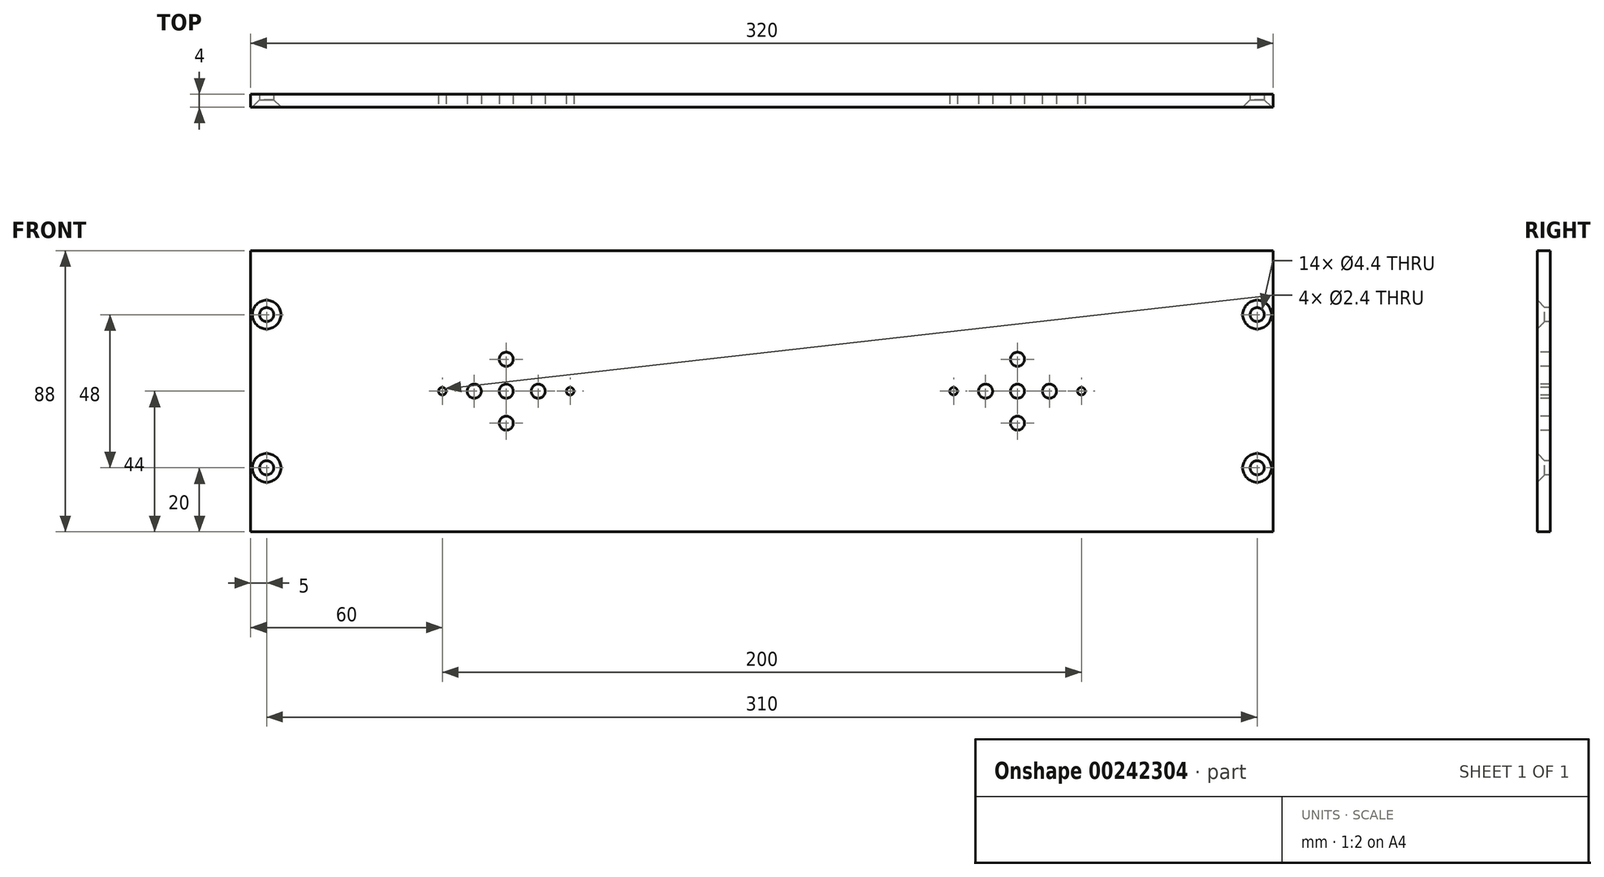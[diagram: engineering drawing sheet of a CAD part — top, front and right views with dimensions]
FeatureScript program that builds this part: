
annotation { "Feature Type Name" : "Feature", "Feature Type Description" : "" }
export const myFeature = defineFeature(function(context is Context, id is Id, definition is map)
    precondition{}
    {
        {
            var Q0;
            Q0=qCreatedBy(makeId("Front.planeOp"),FACE);
            var sketch = newSketch(context, id + "F0", { "sketchPlane" : qUnion([Q0])});
            skLineSegment(sketch, "E0.bottom", {"start": v(160, -44) * mm, "end": v(-160, -44) * mm});
            skLineSegment(sketch, "E0.top", {"start": v(160, 44) * mm, "end": v(-160, 44) * mm});
            skLineSegment(sketch, "E0.left", {"start": v(160, -44) * mm, "end": v(160, 44) * mm});
            skLineSegment(sketch, "E0.right", {"start": v(-160, -44) * mm, "end": v(-160, 44) * mm});
            skPoint(sketch, "E0.middle", {"position": v(0, 0) * mm});
            skSolve(sketch);
        }
        {
            var Q0;
            Q0=makeQuery(id+"F0.imprint","IMPRINT",FACE,{"disambiguationData":[TD([[makeQuery(id+"F0.imprint","IMPRINT",EDGE,{"derivedFrom":sQuery(id+"F0.wireOp",EDGE,"E0.bottom")}),-1.0]])]});
            extrude(context, id + "F1", {"entities" : qUnion([Q0]), "endBound" : BoundingType.SYMMETRIC, "depth" : 4 * mm});
        }
        {
            var Q0;
            Q0=makeQuery(id+"F1.opExtrude","CAP_FACE",FACE,{"disambiguationData":[OSD([sQuery(id+"F0.wireOp",EDGE,"E0.bottom"),sQuery(id+"F0.wireOp",EDGE,"E0.top"),sQuery(id+"F0.wireOp",EDGE,"E0.left"),sQuery(id+"F0.wireOp",EDGE,"E0.right")])],"isStart":false});
            var sketch = newSketch(context, id + "F2", { "sketchPlane" : qUnion([Q0])});
            skCircle(sketch, "E1", {"center": v(-155, -24) * mm, "radius": 2 * mm});
            skCircle(sketch, "E2.0.1.0", {"center": v(-155, 24) * mm, "radius": 2 * mm});
            skCircle(sketch, "E2.1.0.0", {"center": v(155, -24) * mm, "radius": 2 * mm});
            skCircle(sketch, "E2.1.1.0", {"center": v(155, 24) * mm, "radius": 2 * mm});
            skLineSegment(sketch, "E2.direction1", {"start": v(-155, -24) * mm, "end": v(155, -24) * mm, "construction": true});
            skLineSegment(sketch, "E2.direction2", {"start": v(-155, -24) * mm, "end": v(-155, 24) * mm, "construction": true});
            skSolve(sketch);
        }
        {
            var Q0;
            Q0=sQuery(id+"F2.wireOp",VERTEX,"E2.1.1.0.center");
            var Q1;
            Q1=sQuery(id+"F2.wireOp",VERTEX,"E2.1.0.0.center");
            var Q2;
            Q2=sQuery(id+"F2.wireOp",VERTEX,"E1.center");
            var Q3;
            Q3=sQuery(id+"F2.wireOp",VERTEX,"E2.0.1.0.center");
            var Q4;
            Q4=makeQuery(id+"F1.opExtrude","SWEPT_BODY",BODY,{"disambiguationData":[OSD([sQuery(id+"F0.wireOp",EDGE,"E0.bottom"),sQuery(id+"F0.wireOp",EDGE,"E0.top"),sQuery(id+"F0.wireOp",EDGE,"E0.left"),sQuery(id+"F0.wireOp",EDGE,"E0.right")])]});
            hole(context, id + "F3", {"style" : HoleStyle.C_SINK, "endStyle" : HoleEndStyle.BLIND, "standardTappedOrClearance" : lookupTablePath({ "standard" : "ISO", "fit" : "Normal", "size" : "M4", "type" : "Clearance" }), "standardBlindInLast" : lookupTablePath({ "fit" : "Standard", "standard" : "ISO", "size" : "M4", "type" : "Clearance" }), "holeDiameter" : 4.4 * mm, "cSinkDiameter" : 8.96 * mm, "cSinkAngle" : 90 * degree, "holeDepth" : 17.25 * mm, "tappedDepth" : 15 * mm, "tapClearance" : 3, "locations" : qUnion([Q0, Q1, Q2, Q3]), "scope" : qUnion([Q4])});
        }
        {
            var Q0;
            Q0=makeQuery(id+"F1.opExtrude","CAP_FACE",FACE,{"disambiguationData":[OSD([sQuery(id+"F0.wireOp",EDGE,"E0.bottom"),sQuery(id+"F0.wireOp",EDGE,"E0.top"),sQuery(id+"F0.wireOp",EDGE,"E0.left"),sQuery(id+"F0.wireOp",EDGE,"E0.right")])],"isStart":false});
            var sketch = newSketch(context, id + "F4", { "sketchPlane" : qUnion([Q0])});
            skCircle(sketch, "E3", {"center": v(-100, 0) * mm, "radius": 1.5 * mm});
            skCircle(sketch, "E4", {"center": v(-90, 0) * mm, "radius": 2 * mm});
            skCircle(sketch, "E5", {"center": v(-80, 0) * mm, "radius": 2 * mm});
            skCircle(sketch, "E6", {"center": v(-70, 0) * mm, "radius": 2 * mm});
            skCircle(sketch, "E7", {"center": v(-60, 0) * mm, "radius": 1.5 * mm});
            skCircle(sketch, "E8", {"center": v(-80, 10) * mm, "radius": 2 * mm});
            skCircle(sketch, "E9", {"center": v(-80, -10) * mm, "radius": 2 * mm});
            skCircle(sketch, "E10.MirrorC", {"center": v(60, 0) * mm, "radius": 1.5 * mm});
            skCircle(sketch, "E11.MirrorC", {"center": v(70, 0) * mm, "radius": 2 * mm});
            skCircle(sketch, "E12.MirrorC", {"center": v(80, 10) * mm, "radius": 2 * mm});
            skCircle(sketch, "E13.MirrorC", {"center": v(80, 0) * mm, "radius": 2 * mm});
            skCircle(sketch, "E14.MirrorC", {"center": v(80, -10) * mm, "radius": 2 * mm});
            skCircle(sketch, "E15.MirrorC", {"center": v(90, 0) * mm, "radius": 2 * mm});
            skCircle(sketch, "E16.MirrorC", {"center": v(100, 0) * mm, "radius": 1.5 * mm});
            skSolve(sketch);
        }
        {
            var Q0;
            Q0=sQuery(id+"F4.wireOp",VERTEX,"E3.center");
            var Q1;
            Q1=sQuery(id+"F4.wireOp",VERTEX,"E7.center");
            var Q2;
            Q2=sQuery(id+"F4.wireOp",VERTEX,"E10.MirrorC.center");
            var Q3;
            Q3=sQuery(id+"F4.wireOp",VERTEX,"E16.MirrorC.center");
            var Q4;
            Q4=makeQuery(id+"F1.opExtrude","SWEPT_BODY",BODY,{"disambiguationData":[OSD([sQuery(id+"F0.wireOp",EDGE,"E0.bottom"),sQuery(id+"F0.wireOp",EDGE,"E0.top"),sQuery(id+"F0.wireOp",EDGE,"E0.left"),sQuery(id+"F0.wireOp",EDGE,"E0.right")])]});
            hole(context, id + "F5", {"style" : HoleStyle.SIMPLE, "endStyle" : HoleEndStyle.THROUGH, "standardTappedOrClearance" : lookupTablePath({ "standard" : "ISO", "engagement" : "75%", "pitch" : "0.6 mm", "size" : "M3", "type" : "Tapped" }), "standardBlindInLast" : lookupTablePath({ "standard" : "ISO", "engagement" : "75%", "pitch" : "0.6 mm", "size" : "M3", "type" : "Tapped" }), "holeDiameter" : 2.4 * mm, "showTappedDepth" : true, "tappedDepth" : 15 * mm, "tapClearance" : 3, "locations" : qUnion([Q0, Q1, Q2, Q3]), "scope" : qUnion([Q4])});
        }
        {
            var Q0;
            Q0=sQuery(id+"F4.wireOp",VERTEX,"E4.center");
            var Q1;
            Q1=sQuery(id+"F4.wireOp",VERTEX,"E8.center");
            var Q2;
            Q2=sQuery(id+"F4.wireOp",VERTEX,"E5.center");
            var Q3;
            Q3=sQuery(id+"F4.wireOp",VERTEX,"E9.center");
            var Q4;
            Q4=sQuery(id+"F4.wireOp",VERTEX,"E6.center");
            var Q5;
            Q5=sQuery(id+"F4.wireOp",VERTEX,"E11.MirrorC.center");
            var Q6;
            Q6=sQuery(id+"F4.wireOp",VERTEX,"E13.MirrorC.center");
            var Q7;
            Q7=sQuery(id+"F4.wireOp",VERTEX,"E15.MirrorC.center");
            var Q8;
            Q8=sQuery(id+"F4.wireOp",VERTEX,"E12.MirrorC.center");
            var Q9;
            Q9=sQuery(id+"F4.wireOp",VERTEX,"E14.MirrorC.center");
            var Q10;
            Q10=makeQuery(id+"F1.opExtrude","SWEPT_BODY",BODY,{"disambiguationData":[OSD([sQuery(id+"F0.wireOp",EDGE,"E0.bottom"),sQuery(id+"F0.wireOp",EDGE,"E0.top"),sQuery(id+"F0.wireOp",EDGE,"E0.left"),sQuery(id+"F0.wireOp",EDGE,"E0.right")])]});
            hole(context, id + "F6", {"style" : HoleStyle.SIMPLE, "endStyle" : HoleEndStyle.THROUGH, "standardTappedOrClearance" : lookupTablePath({ "standard" : "ISO", "fit" : "Normal", "size" : "M4", "type" : "Clearance" }), "standardBlindInLast" : lookupTablePath({ "fit" : "Standard", "standard" : "ISO", "size" : "M4", "type" : "Clearance" }), "holeDiameter" : 4.4 * mm, "tappedDepth" : 15 * mm, "tapClearance" : 3, "locations" : qUnion([Q0, Q1, Q2, Q3, Q4, Q5, Q6, Q7, Q8, Q9]), "scope" : qUnion([Q10])});
        }
    });
